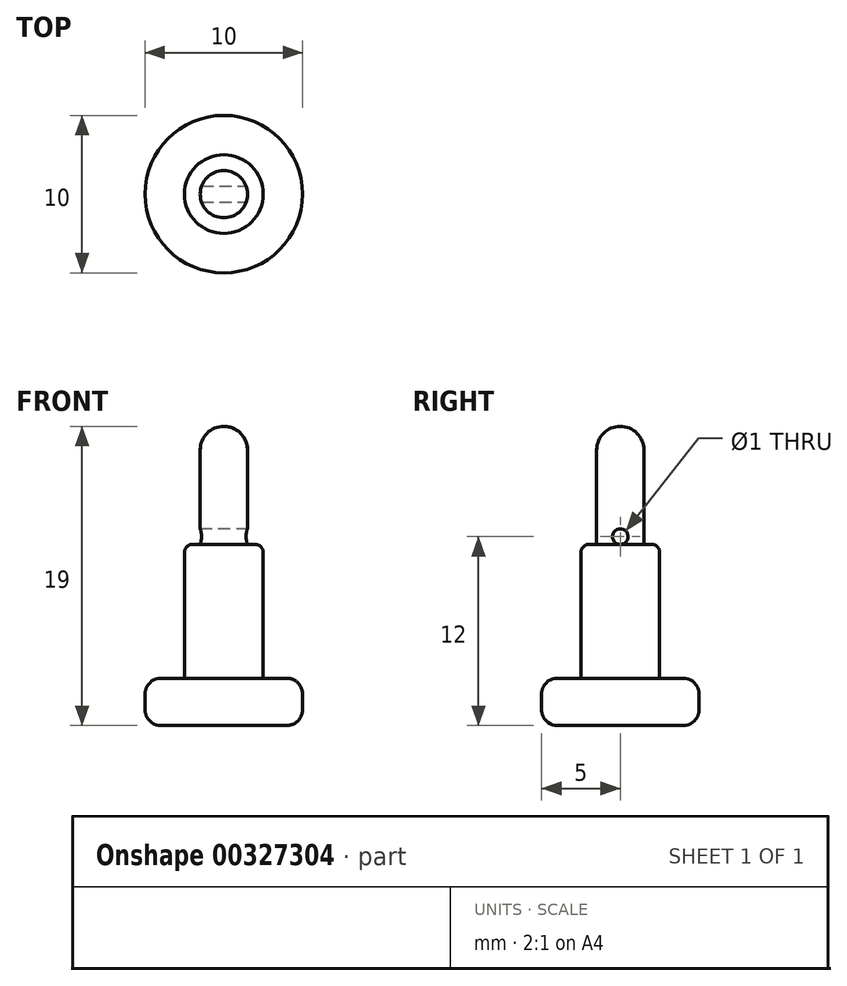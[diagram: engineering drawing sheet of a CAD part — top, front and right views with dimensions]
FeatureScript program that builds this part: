
annotation { "Feature Type Name" : "Feature", "Feature Type Description" : "" }
export const myFeature = defineFeature(function(context is Context, id is Id, definition is map)
    precondition{}
    {
        {
            var Q0;
            Q0=qCreatedBy(makeId("Top.planeOp"),FACE);
            var sketch = newSketch(context, id + "F0", { "sketchPlane" : qUnion([Q0])});
            skCircle(sketch, "E0", {"center": v(0, 0) * mm, "radius": 5 * mm});
            skSolve(sketch);
        }
        {
            var Q0;
            Q0 = qSketchRegion(id + "F0", true);
            extrude(context, id + "F1", {"entities" : qUnion([Q0]), "depth" : 3 * mm, "offsetDistance" : 25 * mm});
        }
        {
            var Q0;
            Q0=makeQuery(id+"F1.opExtrude","CAP_FACE",FACE,{"disambiguationData":[OSD([sQuery(id+"F0.wireOp",EDGE,"E0")])],"isStart":false});
            var sketch = newSketch(context, id + "F2", { "sketchPlane" : qUnion([Q0])});
            skCircle(sketch, "E1", {"center": v(0, 0) * mm, "radius": 2.5 * mm});
            skSolve(sketch);
        }
        {
            var Q0;
            Q0 = qSketchRegion(id + "F2", true);
            extrude(context, id + "F3", {"entities" : qUnion([Q0]), "operationType" : NewBodyOperationType.ADD, "depth" : 8.5 * mm, "offsetDistance" : 25 * mm});
        }
        {
            var Q0;
            Q0=makeQuery(id+"F3.opExtrude","CAP_FACE",FACE,{"disambiguationData":[OSD([sQuery(id+"F2.wireOp",EDGE,"E1")])],"isStart":false});
            var sketch = newSketch(context, id + "F4", { "sketchPlane" : qUnion([Q0])});
            skCircle(sketch, "E2", {"center": v(0, 0) * mm, "radius": 1.5 * mm});
            skSolve(sketch);
        }
        {
            var Q0;
            Q0 = qSketchRegion(id + "F4", true);
            extrude(context, id + "F5", {"entities" : qUnion([Q0]), "operationType" : NewBodyOperationType.ADD, "depth" : 7.5 * mm, "offsetDistance" : 25 * mm});
        }
        {
            var Q0;
            Q0=makeQuery(id+"F5.opExtrude","CAP_FACE",FACE,{"disambiguationData":[OSD([sQuery(id+"F4.wireOp",EDGE,"E2")])],"isStart":false});
            fillet(context, id + "F6", {"entities" : qUnion([Q0]), "radius" : 1.5 * mm, "tangentPropagation" : true, "allowEdgeOverflow" : false});
        }
        {
            var Q0;
            Q0=makeQuery(id+"F3.opExtrude","CAP_EDGE",EDGE,{"disambiguationData":[OSD([sQuery(id+"F2.wireOp",EDGE,"E1")])],"isStart":true});
            var Q1;
            Q1=makeQuery(id+"F1.opExtrude","CAP_EDGE",EDGE,{"disambiguationData":[OSD([sQuery(id+"F0.wireOp",EDGE,"E0")])],"isStart":true});
            var Q2;
            Q2=makeQuery(id+"F1.opExtrude","CAP_EDGE",EDGE,{"disambiguationData":[OSD([sQuery(id+"F0.wireOp",EDGE,"E0")])],"isStart":false});
            fillet(context, id + "F7", {"entities" : qUnion([Q0, Q1, Q2]), "radius" : 1 * mm, "tangentPropagation" : true, "allowEdgeOverflow" : false});
        }
        {
            var Q0;
            Q0=makeQuery(id+"F5.opExtrude","CAP_EDGE",EDGE,{"disambiguationData":[OSD([sQuery(id+"F4.wireOp",EDGE,"E2")])],"isStart":true});
            var Q1;
            Q1=makeQuery(id+"F3.opExtrude","CAP_EDGE",EDGE,{"disambiguationData":[OSD([sQuery(id+"F2.wireOp",EDGE,"E1")])],"isStart":false});
            fillet(context, id + "F8", {"entities" : qUnion([Q0, Q1]), "radius" : .5 * mm, "tangentPropagation" : true, "allowEdgeOverflow" : false});
        }
        {
            var Q0;
            Q0=qCreatedBy(makeId("Right.planeOp"),FACE);
            var sketch = newSketch(context, id + "F9", { "sketchPlane" : qUnion([Q0])});
            skCircle(sketch, "E3", {"center": v(0, 12) * mm, "radius": 0.5 * mm});
            skLineSegment(sketch, "E4.0", {"start": v(-2, 11.5) * mm, "end": v(2, 11.5) * mm});
            skSolve(sketch);
        }
        {
            var Q0;
            Q0 = qSketchRegion(id + "F9", true);
            extrude(context, id + "F10", {"entities" : qUnion([Q0]), "operationType" : NewBodyOperationType.REMOVE, "endBound" : BoundingType.SYMMETRIC, "oppositeDirection" : true, "depth" : 5 * mm, "offsetDistance" : 25 * mm});
        }
    });
